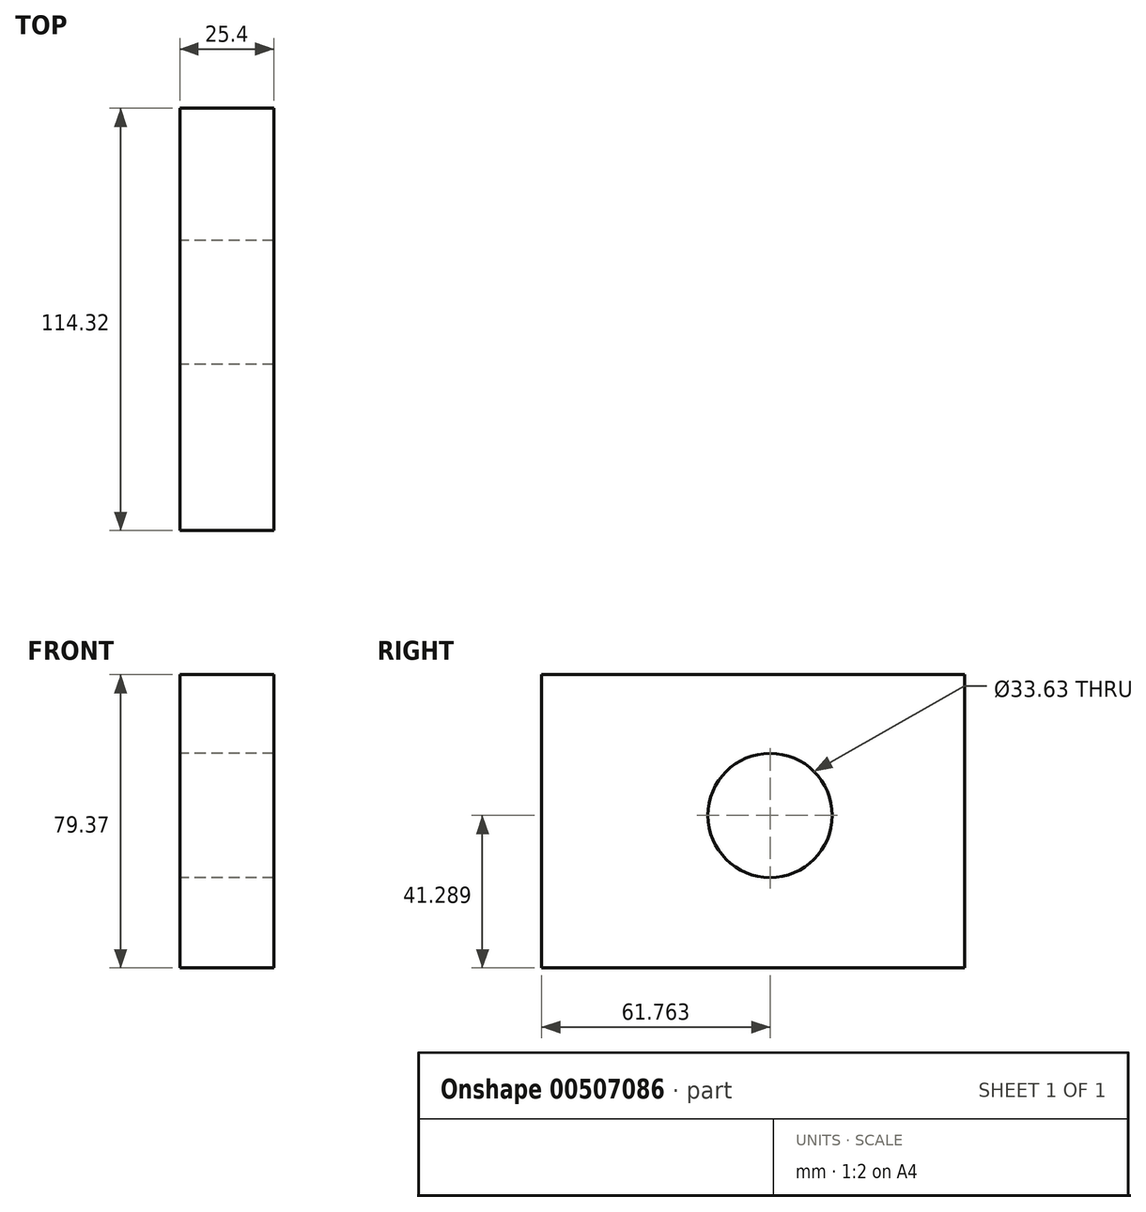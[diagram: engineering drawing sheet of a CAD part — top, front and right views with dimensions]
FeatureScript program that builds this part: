
annotation { "Feature Type Name" : "Feature", "Feature Type Description" : "" }
export const myFeature = defineFeature(function(context is Context, id is Id, definition is map)
    precondition{}
    {
        {
            var Q0;
            Q0=qCreatedBy(makeId("Right.planeOp"),FACE);
            var sketch = newSketch(context, id + "F0", { "sketchPlane" : qUnion([Q0])});
            skLineSegment(sketch, "E0.bottom", {"start": v(-87.77, 110.05) * mm, "end": v(26.55, 110.05) * mm});
            skLineSegment(sketch, "E0.top", {"start": v(-87.77, 30.68) * mm, "end": v(26.55, 30.68) * mm});
            skLineSegment(sketch, "E0.left", {"start": v(-87.77, 110.05) * mm, "end": v(-87.77, 30.68) * mm});
            skLineSegment(sketch, "E0.right", {"start": v(26.55, 110.05) * mm, "end": v(26.55, 30.68) * mm});
            skCircle(sketch, "E1", {"center": v(-26, 71.97) * mm, "radius": 16.81 * mm});
            skSolve(sketch);
        }
        {
            var Q0;
            Q0=makeQuery(id+"F0.imprint","IMPRINT",FACE,{"disambiguationData":[TD([[makeQuery(id+"F0.imprint","IMPRINT",EDGE,{"derivedFrom":sQuery(id+"F0.wireOp",EDGE,"E0.bottom")}),-1.0]])]});
            extrude(context, id + "F1", {"entities" : qUnion([Q0]), "depth" : 25.4 * mm});
        }
    });
